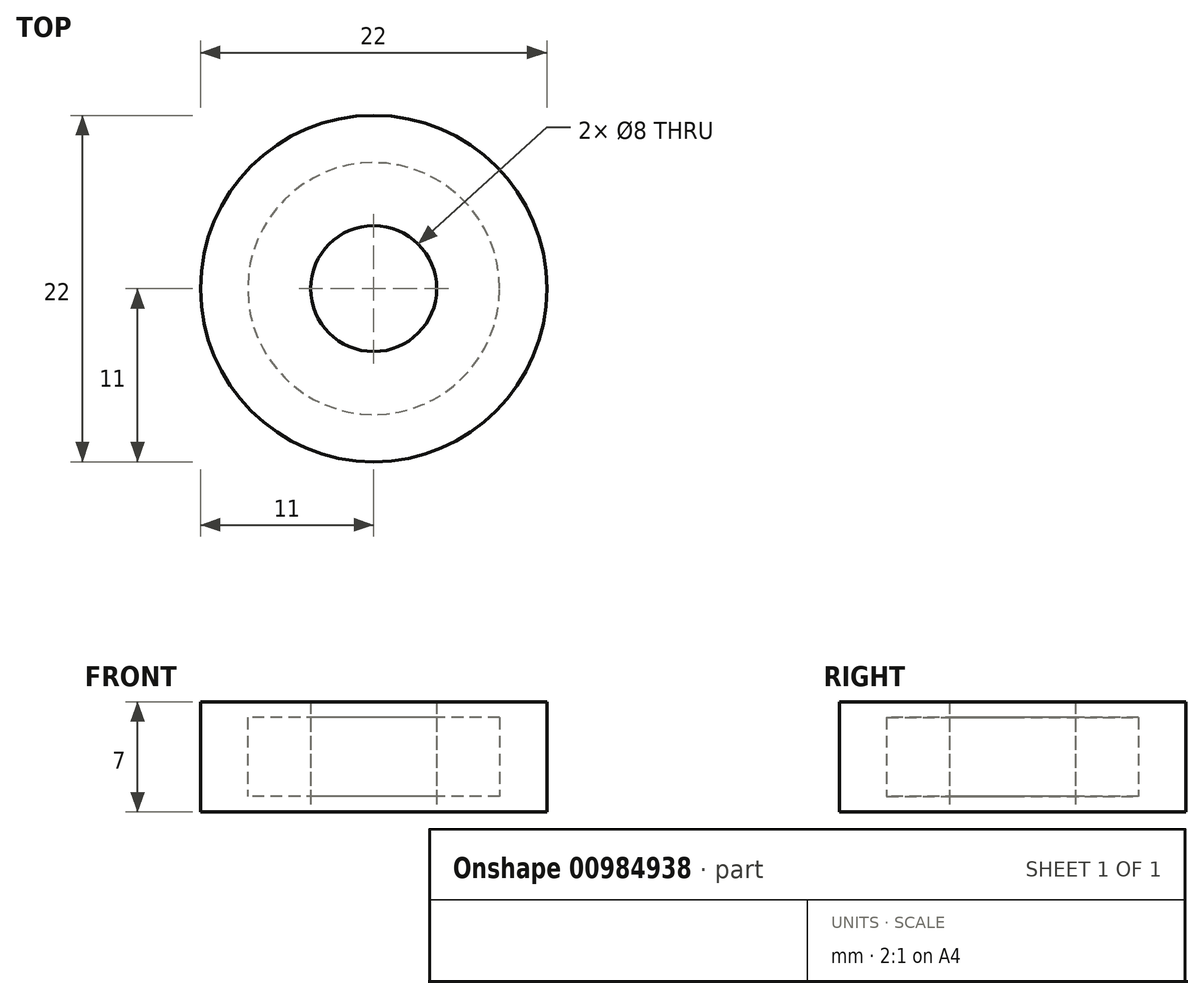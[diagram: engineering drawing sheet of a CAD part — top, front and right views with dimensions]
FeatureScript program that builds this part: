
annotation { "Feature Type Name" : "Feature", "Feature Type Description" : "" }
export const myFeature = defineFeature(function(context is Context, id is Id, definition is map)
    precondition{}
    {
        {
            var Q0;
            Q0=qCreatedBy(makeId("Top.planeOp"),FACE);
            var sketch = newSketch(context, id + "F0", { "sketchPlane" : qUnion([Q0])});
            skCircle(sketch, "E0", {"center": v(0, 0) * mm, "radius": 11 * mm});
            skCircle(sketch, "E1", {"center": v(0, 0) * mm, "radius": 4 * mm});
            skSolve(sketch);
        }
        {
            var Q0;
            Q0 = qSketchRegion(id + "F0", true);
            extrude(context, id + "F1", {"entities" : qUnion([Q0]), "endBound" : BoundingType.SYMMETRIC, "depth" : 7 * mm, "offsetDistance" : 25 * mm});
        }
        {
            var Q0;
            Q0=qCreatedBy(makeId("Top.planeOp"),FACE);
            var sketch = newSketch(context, id + "F2", { "sketchPlane" : qUnion([Q0])});
            skCircle(sketch, "E2", {"center": v(0, 0) * mm, "radius": 8 * mm});
            skCircle(sketch, "E3", {"center": v(0, 0) * mm, "radius": 4 * mm});
            skSolve(sketch);
        }
        {
            var Q0;
            Q0 = qSketchRegion(id + "F2", true);
            extrude(context, id + "F3", {"entities" : qUnion([Q0]), "endBound" : BoundingType.SYMMETRIC, "depth" : 5 * mm, "offsetDistance" : 25 * mm});
        }
    });
